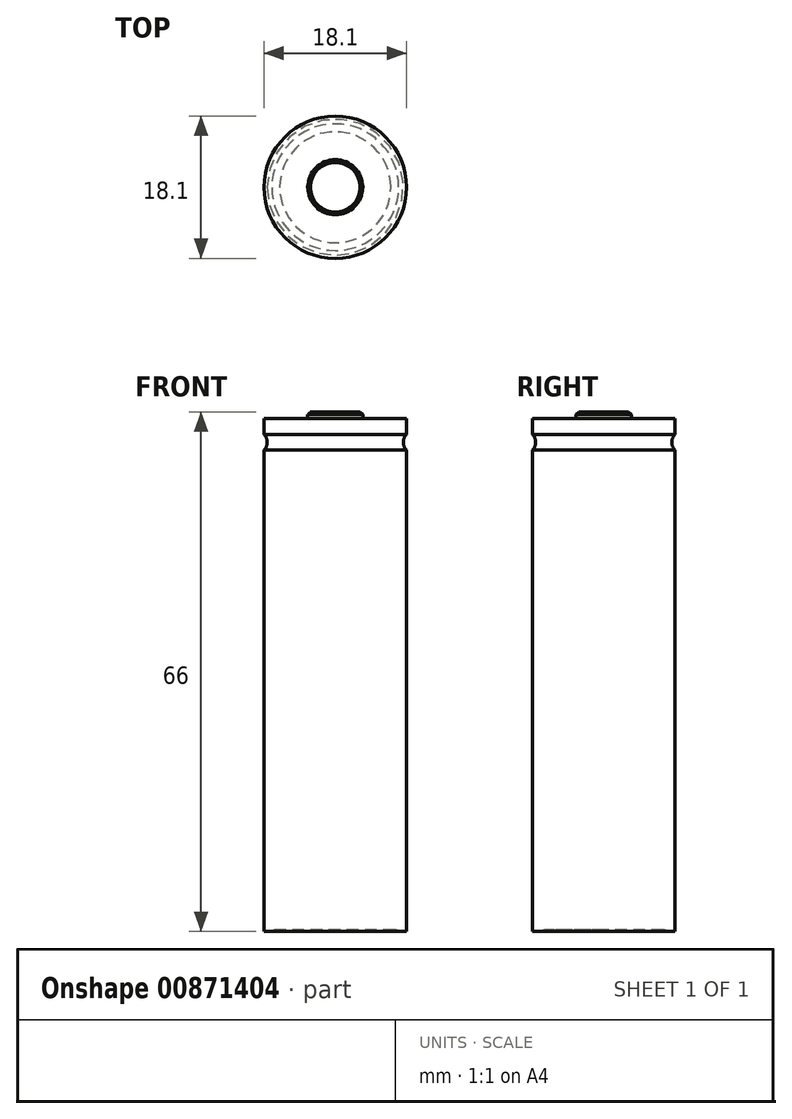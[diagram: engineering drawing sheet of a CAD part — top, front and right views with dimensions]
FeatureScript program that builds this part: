
annotation { "Feature Type Name" : "Feature", "Feature Type Description" : "" }
export const myFeature = defineFeature(function(context is Context, id is Id, definition is map)
    precondition{}
    {
        {
            var Q0;
            Q0=qCreatedBy(makeId("Front.planeOp"),FACE);
            var sketch = newSketch(context, id + "F0", { "sketchPlane" : qUnion([Q0])});
            skLineSegment(sketch, "E0", {"start": v(0, 0) * mm, "end": v(0, 66) * mm});
            skLineSegment(sketch, "E1", {"start": v(0, 66) * mm, "end": v(3.15, 66) * mm});
            skLineSegment(sketch, "E2", {"start": v(3.15, 66) * mm, "end": v(3.5, 65.65) * mm});
            skLineSegment(sketch, "E3", {"start": v(3.5, 65.65) * mm, "end": v(3.5, 65.15) * mm});
            skLineSegment(sketch, "E4", {"start": v(3.5, 65.15) * mm, "end": v(9.05, 65.15) * mm});
            skLineSegment(sketch, "E5", {"start": v(9.05, 65.15) * mm, "end": v(9.05, 63.15) * mm});
            skArc(sketch, "E6", {"start": v(9.05, 63.15) * mm, "mid": v(8.65, 62.15) * mm, "end": v(9.05, 61.15) * mm});
            skLineSegment(sketch, "E7", {"start": v(9.05, 61.15) * mm, "end": v(9.05, 0) * mm});
            skLineSegment(sketch, "E8", {"start": v(9.05, 0) * mm, "end": v(8.05, 0) * mm});
            skArc(sketch, "E9", {"start": v(8.05, 0) * mm, "mid": v(7.55, 0.2) * mm, "end": v(7.05, 0) * mm});
            skLineSegment(sketch, "E10.trimOffspring", {"start": v(7.05, 0) * mm, "end": v(0, 0) * mm});
            skSolve(sketch);
        }
        {
            var Q0;
            Q0=makeQuery(id+"F0.imprint","IMPRINT",FACE,{"disambiguationData":[TD([[makeQuery(id+"F0.imprint","IMPRINT",EDGE,{"derivedFrom":sQuery(id+"F0.wireOp",EDGE,"E0")}),-1.0]])]});
            var Q1;
            Q1=sQuery(id+"F0.wireOp",EDGE,"E0");
            revolve(context, id + "F1", {"surfaceOperationType" : NewSurfaceOperationType.NEW, "entities" : qUnion([Q0]), "axis" : qUnion([Q1]), "revolveType" : RevolveType.FULL});
        }
    });
